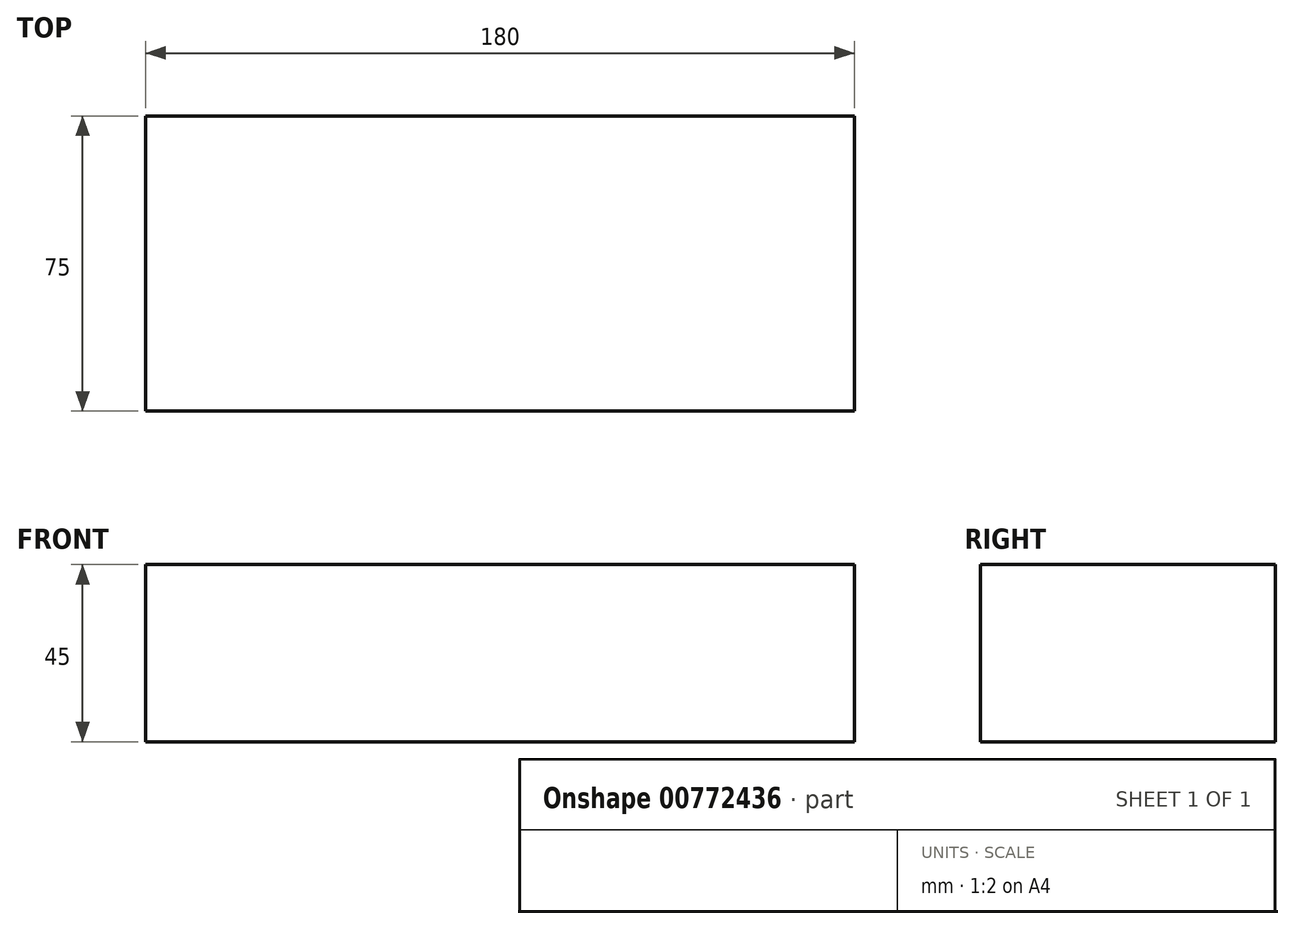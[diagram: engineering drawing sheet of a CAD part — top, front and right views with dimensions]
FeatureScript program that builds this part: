
annotation { "Feature Type Name" : "Feature", "Feature Type Description" : "" }
export const myFeature = defineFeature(function(context is Context, id is Id, definition is map)
    precondition{}
    {
        {
            var Q0;
            Q0=qCreatedBy(makeId("Top.planeOp"),FACE);
            var sketch = newSketch(context, id + "F0", { "sketchPlane" : qUnion([Q0])});
            skLineSegment(sketch, "E0.bottom", {"start": v(0, 0) * mm, "end": v(180, 0) * mm});
            skLineSegment(sketch, "E0.top", {"start": v(0, 75) * mm, "end": v(180, 75) * mm});
            skLineSegment(sketch, "E0.left", {"start": v(0, 0) * mm, "end": v(0, 75) * mm});
            skLineSegment(sketch, "E0.right", {"start": v(180, 0) * mm, "end": v(180, 75) * mm});
            skSolve(sketch);
        }
        {
            var Q0;
            Q0=makeQuery(id+"F0.imprint","IMPRINT",FACE,{"disambiguationData":[TD([[makeQuery(id+"F0.imprint","IMPRINT",EDGE,{"derivedFrom":sQuery(id+"F0.wireOp",EDGE,"E0.bottom")}),1.0]])]});
            extrude(context, id + "F1", {"entities" : qUnion([Q0]), "depth" : 45 * mm, "offsetDistance" : 25 * mm});
        }
    });
